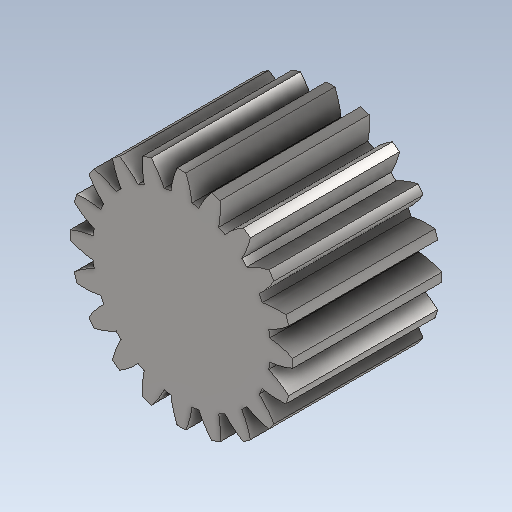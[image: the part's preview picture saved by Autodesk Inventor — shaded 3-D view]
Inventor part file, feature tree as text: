
AUTODESK INVENTOR PART (.ipt)
format: ipt  version: 2020.5 (Build 245400000, 400)  size: 283,648 bytes
history: native  units: mm (DEFAULTED — no unit token found)
features: plane x3, other x3, sketch x2, extrude x1
ambient origin geometry x8: Origin, YZ Plane, XZ Plane, XY Plane, X Axis, Y Axis, Z Axis, Center Point
bodies: Solid1 (feature_tree)
feature tree (9):
  extrude  "Extrusion1"  Depth=30.0mm TaperAngle=0.0deg
  plane  "Work Plane2"
  plane  "Work Plane8"
  plane  "Work Plane9"
  other  "Engranaje recto"
  sketch  "Sketch1"  dims[d0=44.8mm d1=30.0mm d2=0.0mm]
  sketch  "Sketch2"  dims[d3=40.0mm d4=10.0mm d5=0.0mm d16=82.0mm d17=0.0mm d34=1.570796mm d39=0.0mm d41=0.0mm d43=82.0mm d46=82.0mm d47=0.0mm d48=0.0mm]
  other  "Srf1"
  other  "Diámetro de separación"
